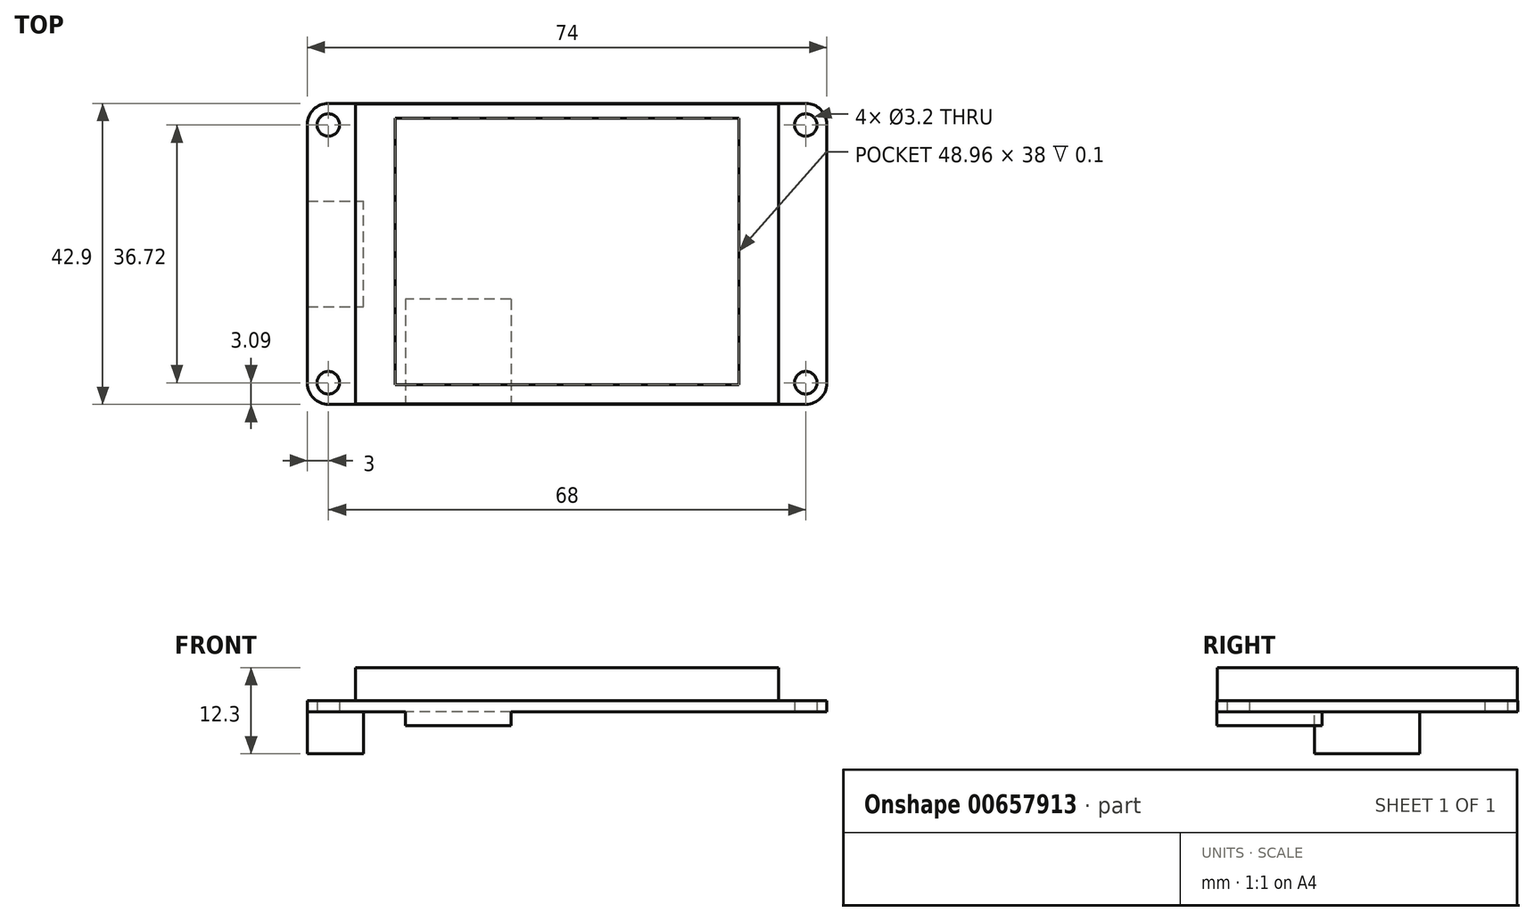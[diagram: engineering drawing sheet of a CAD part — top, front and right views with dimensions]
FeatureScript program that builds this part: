
annotation { "Feature Type Name" : "Feature", "Feature Type Description" : "" }
export const myFeature = defineFeature(function(context is Context, id is Id, definition is map)
    precondition{}
    {
        {
            var Q0;
            Q0=qCreatedBy(makeId("Top.planeOp"),FACE);
            var sketch = newSketch(context, id + "F0", { "sketchPlane" : qUnion([Q0])});
            skLineSegment(sketch, "E0.bottom", {"start": v(37, -21.45) * mm, "end": v(-37, -21.45) * mm});
            skLineSegment(sketch, "E0.top", {"start": v(37, 21.45) * mm, "end": v(-37, 21.45) * mm});
            skLineSegment(sketch, "E0.left", {"start": v(37, -21.45) * mm, "end": v(37, 21.45) * mm});
            skLineSegment(sketch, "E0.right", {"start": v(-37, -21.45) * mm, "end": v(-37, 21.45) * mm});
            skPoint(sketch, "E0.middle", {"position": v(0, 0) * mm});
            skLineSegment(sketch, "E1.bottom", {"start": v(34, 18.36) * mm, "end": v(-34, 18.36) * mm, "construction": true});
            skLineSegment(sketch, "E1.top", {"start": v(34, -18.36) * mm, "end": v(-34, -18.36) * mm, "construction": true});
            skLineSegment(sketch, "E1.left", {"start": v(34, 18.36) * mm, "end": v(34, -18.36) * mm, "construction": true});
            skLineSegment(sketch, "E1.right", {"start": v(-34, 18.36) * mm, "end": v(-34, -18.36) * mm, "construction": true});
            skCircle(sketch, "E2", {"center": v(-34, 18.36) * mm, "radius": 1.6 * mm});
            skCircle(sketch, "E3", {"center": v(-34, -18.36) * mm, "radius": 1.6 * mm});
            skCircle(sketch, "E4", {"center": v(34, 18.36) * mm, "radius": 1.6 * mm});
            skCircle(sketch, "E5", {"center": v(34, -18.36) * mm, "radius": 1.6 * mm});
            skSolve(sketch);
        }
        {
            var Q0;
            Q0=makeQuery(id+"F0.imprint","IMPRINT",FACE,{"disambiguationData":[TD([[makeQuery(id+"F0.imprint","IMPRINT",EDGE,{"derivedFrom":sQuery(id+"F0.wireOp",EDGE,"E0.bottom")}),-1.0]])]});
            extrude(context, id + "F1", {"entities" : qUnion([Q0]), "depth" : 1.6 * mm, "offsetDistance" : 25 * mm});
        }
        {
            var Q0;
            Q0=makeQuery(id+"F1.opExtrude","CAP_FACE",FACE,{"disambiguationData":[OSD([sQuery(id+"F0.wireOp",EDGE,"E0.bottom"),sQuery(id+"F0.wireOp",EDGE,"E0.top"),sQuery(id+"F0.wireOp",EDGE,"E0.left"),sQuery(id+"F0.wireOp",EDGE,"E0.right"),sQuery(id+"F0.wireOp",EDGE,"E2"),sQuery(id+"F0.wireOp",EDGE,"E3"),sQuery(id+"F0.wireOp",EDGE,"E4"),sQuery(id+"F0.wireOp",EDGE,"E5")])],"isStart":false});
            var sketch = newSketch(context, id + "F2", { "sketchPlane" : qUnion([Q0])});
            skLineSegment(sketch, "E6.bottom", {"start": v(-30.13, 21.35) * mm, "end": v(30.13, 21.35) * mm});
            skLineSegment(sketch, "E6.top", {"start": v(-30.13, -21.37) * mm, "end": v(30.13, -21.37) * mm});
            skLineSegment(sketch, "E6.left", {"start": v(-30.13, 21.35) * mm, "end": v(-30.13, -21.37) * mm});
            skLineSegment(sketch, "E6.right", {"start": v(30.13, 21.35) * mm, "end": v(30.13, -21.37) * mm});
            skLineSegment(sketch, "E7", {"start": v(0, 21.35) * mm, "end": v(0, 0) * mm, "construction": true});
            skSolve(sketch);
        }
        {
            var Q0;
            Q0=makeQuery(id+"F2.imprint","IMPRINT",FACE,{"disambiguationData":[TD([[makeQuery(id+"F2.imprint","IMPRINT",EDGE,{"derivedFrom":sQuery(id+"F2.wireOp",EDGE,"E6.bottom")}),-1.0]])]});
            extrude(context, id + "F3", {"entities" : qUnion([Q0]), "operationType" : NewBodyOperationType.ADD, "depth" : 4.7 * mm, "offsetDistance" : 25 * mm});
        }
        {
            var Q0;
            Q0=makeQuery(id+"F3.opExtrude","CAP_FACE",FACE,{"disambiguationData":[OSD([sQuery(id+"F2.wireOp",EDGE,"E6.bottom"),sQuery(id+"F2.wireOp",EDGE,"E6.top"),sQuery(id+"F2.wireOp",EDGE,"E6.left"),sQuery(id+"F2.wireOp",EDGE,"E6.right")])],"isStart":false});
            var sketch = newSketch(context, id + "F4", { "sketchPlane" : qUnion([Q0])});
            skLineSegment(sketch, "E8.bottom", {"start": v(-24.48, 19.35) * mm, "end": v(24.48, 19.35) * mm});
            skLineSegment(sketch, "E8.top", {"start": v(-24.48, -18.65) * mm, "end": v(24.48, -18.65) * mm});
            skLineSegment(sketch, "E8.left", {"start": v(-24.48, 19.35) * mm, "end": v(-24.48, -18.65) * mm});
            skLineSegment(sketch, "E8.right", {"start": v(24.48, 19.35) * mm, "end": v(24.48, -18.65) * mm});
            skLineSegment(sketch, "E9", {"start": v(0, 19.35) * mm, "end": v(0, 0) * mm, "construction": true});
            skSolve(sketch);
        }
        {
            var Q0;
            Q0=qSketchRegion(id+"F4",true);
            extrude(context, id + "F5", {"entities" : qUnion([Q0]), "operationType" : NewBodyOperationType.REMOVE, "oppositeDirection" : true, "depth" : .1 * mm});
        }
        {
            var Q0;
            Q0=makeQuery(id+"F1.opExtrude","CAP_FACE",FACE,{"disambiguationData":[OSD([sQuery(id+"F0.wireOp",EDGE,"E0.bottom"),sQuery(id+"F0.wireOp",EDGE,"E0.top"),sQuery(id+"F0.wireOp",EDGE,"E0.left"),sQuery(id+"F0.wireOp",EDGE,"E0.right"),sQuery(id+"F0.wireOp",EDGE,"E2"),sQuery(id+"F0.wireOp",EDGE,"E3"),sQuery(id+"F0.wireOp",EDGE,"E4"),sQuery(id+"F0.wireOp",EDGE,"E5")])],"isStart":true});
            var sketch = newSketch(context, id + "F6", { "sketchPlane" : qUnion([Q0])});
            skLineSegment(sketch, "E10.bottom", {"start": v(-8, 6.45) * mm, "end": v(-23, 6.45) * mm});
            skLineSegment(sketch, "E10.top", {"start": v(-8, 21.45) * mm, "end": v(-23, 21.45) * mm});
            skLineSegment(sketch, "E10.left", {"start": v(-8, 6.45) * mm, "end": v(-8, 21.45) * mm});
            skLineSegment(sketch, "E10.right", {"start": v(-23, 6.45) * mm, "end": v(-23, 21.45) * mm});
            skLineSegment(sketch, "E11.bottom", {"start": v(-37, 7.5) * mm, "end": v(-29, 7.5) * mm});
            skLineSegment(sketch, "E11.top", {"start": v(-37, -7.5) * mm, "end": v(-29, -7.5) * mm});
            skLineSegment(sketch, "E11.left", {"start": v(-37, 7.5) * mm, "end": v(-37, -7.5) * mm});
            skLineSegment(sketch, "E11.right", {"start": v(-29, 7.5) * mm, "end": v(-29, -7.5) * mm});
            skPoint(sketch, "E12", {"position": v(-29, 0) * mm});
            skSolve(sketch);
        }
        {
            var Q0;
            Q0=makeQuery(id+"F6.imprint","IMPRINT",FACE,{"disambiguationData":[TD([[makeQuery(id+"F6.imprint","IMPRINT",EDGE,{"derivedFrom":sQuery(id+"F6.wireOp",EDGE,"E10.bottom")}),-1.0]])]});
            extrude(context, id + "F7", {"entities" : qUnion([Q0]), "operationType" : NewBodyOperationType.ADD, "depth" : 2 * mm});
        }
        {
            var Q0;
            Q0=makeQuery(id+"F6.imprint","IMPRINT",FACE,{"disambiguationData":[TD([[makeQuery(id+"F6.imprint","IMPRINT",EDGE,{"derivedFrom":sQuery(id+"F6.wireOp",EDGE,"E11.bottom")}),-1.0]])]});
            extrude(context, id + "F8", {"entities" : qUnion([Q0]), "operationType" : NewBodyOperationType.ADD, "depth" : 6 * mm});
        }
        {
            var Q0;
            Q0=makeQuery(id+"F1.opExtrude","SWEPT_EDGE",EDGE,{"disambiguationData":[OSD([sQuery(id+"F0.wireOp",EDGE,"E0.top"),sQuery(id+"F0.wireOp",EDGE,"E0.left")])]});
            var Q1;
            Q1=makeQuery(id+"F1.opExtrude","SWEPT_EDGE",EDGE,{"disambiguationData":[OSD([sQuery(id+"F0.wireOp",EDGE,"E0.bottom"),sQuery(id+"F0.wireOp",EDGE,"E0.left")])]});
            var Q2;
            Q2=makeQuery(id+"F1.opExtrude","SWEPT_EDGE",EDGE,{"disambiguationData":[OSD([sQuery(id+"F0.wireOp",EDGE,"E0.bottom"),sQuery(id+"F0.wireOp",EDGE,"E0.right")])]});
            var Q3;
            Q3=makeQuery(id+"F1.opExtrude","SWEPT_EDGE",EDGE,{"disambiguationData":[OSD([sQuery(id+"F0.wireOp",EDGE,"E0.top"),sQuery(id+"F0.wireOp",EDGE,"E0.right")])]});
            fillet(context, id + "F9", {"entities" : qUnion([Q0, Q1, Q2, Q3]), "radius" : 3 * mm, "tangentPropagation" : true, "allowEdgeOverflow" : false});
        }
    });
